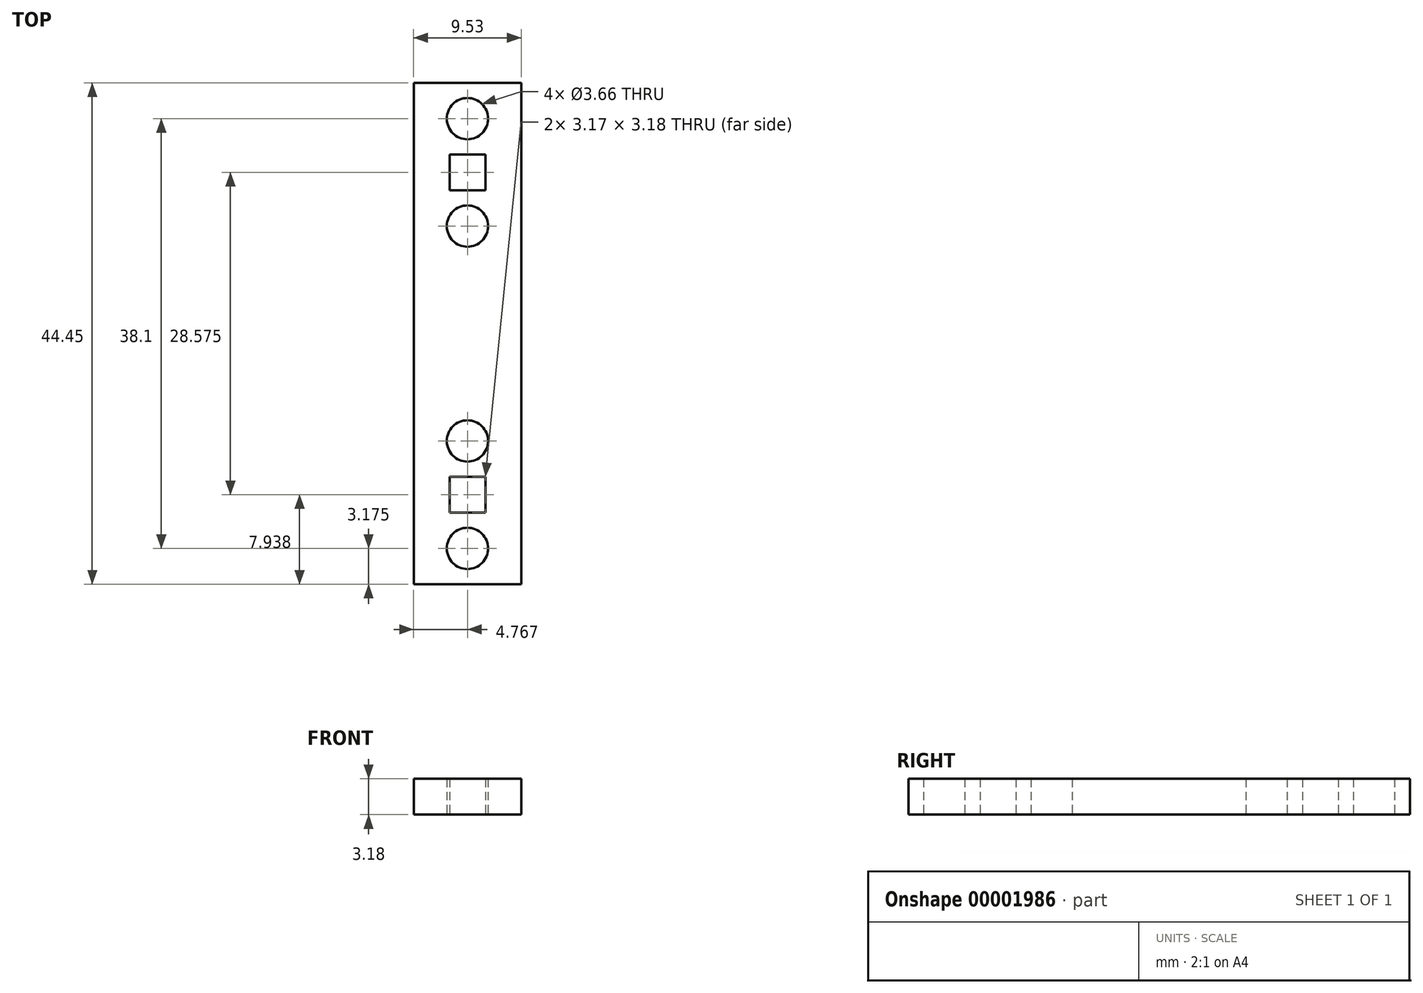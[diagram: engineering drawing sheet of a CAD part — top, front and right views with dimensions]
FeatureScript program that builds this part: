
annotation { "Feature Type Name" : "Feature", "Feature Type Description" : "" }
export const myFeature = defineFeature(function(context is Context, id is Id, definition is map)
    precondition{}
    {
        {
            var Q0;
            Q0=qCreatedBy(makeId("Top.planeOp"),FACE);
            var sketch = newSketch(context, id + "F0", { "sketchPlane" : qUnion([Q0])});
            skLineSegment(sketch, "E0", {"start": v(0, -6.35) * mm, "end": v(0, -38.1) * mm});
            skLineSegment(sketch, "E1", {"start": v(-3.18, -38.1) * mm, "end": v(-3.18, -34.93) * mm});
            skLineSegment(sketch, "E2", {"start": v(-3.18, -6.35) * mm, "end": v(-6.35, -6.35) * mm});
            skLineSegment(sketch, "E3", {"start": v(-6.35, -6.35) * mm, "end": v(-6.35, -9.52) * mm});
            skLineSegment(sketch, "E4", {"start": v(-9.52, -38.1) * mm, "end": v(-9.52, -6.35) * mm});
            skLineSegment(sketch, "E5", {"start": v(-9.52, -6.35) * mm, "end": v(-9.52, 0) * mm});
            skLineSegment(sketch, "E6", {"start": v(-9.52, 0) * mm, "end": v(0, 0) * mm});
            skLineSegment(sketch, "E7", {"start": v(-6.35, -9.52) * mm, "end": v(-3.18, -9.52) * mm});
            skLineSegment(sketch, "E8", {"start": v(-6.35, -38.1) * mm, "end": v(-3.18, -38.1) * mm});
            skLineSegment(sketch, "E9", {"start": v(-3.18, -34.93) * mm, "end": v(-6.35, -34.93) * mm});
            skLineSegment(sketch, "E10", {"start": v(-9.52, -38.1) * mm, "end": v(-9.52, -44.45) * mm});
            skLineSegment(sketch, "E11", {"start": v(-9.52, -44.45) * mm, "end": v(0, -44.45) * mm});
            skLineSegment(sketch, "E12", {"start": v(0, -6.35) * mm, "end": v(0, 0) * mm});
            skLineSegment(sketch, "E13", {"start": v(0, -38.1) * mm, "end": v(0, -44.45) * mm});
            skLineSegment(sketch, "E14.trimOffspring", {"start": v(-6.35, -34.93) * mm, "end": v(-6.35, -38.1) * mm});
            skLineSegment(sketch, "E15.trimOffspring", {"start": v(-3.18, -9.52) * mm, "end": v(-3.18, -6.35) * mm});
            skLineSegment(sketch, "E16", {"start": v(-9.52, -3.17) * mm, "end": v(-4.76, -3.17) * mm, "construction": true});
            skLineSegment(sketch, "E17", {"start": v(-4.76, -3.17) * mm, "end": v(0, -3.17) * mm, "construction": true});
            skCircle(sketch, "E18", {"center": v(-4.76, -3.17) * mm, "radius": 1.83 * mm});
            skLineSegment(sketch, "E19", {"start": v(0, -41.27) * mm, "end": v(-4.76, -41.27) * mm, "construction": true});
            skLineSegment(sketch, "E20", {"start": v(-4.76, -41.27) * mm, "end": v(-9.52, -41.27) * mm, "construction": true});
            skCircle(sketch, "E21", {"center": v(-4.76, -41.27) * mm, "radius": 1.83 * mm});
            skLineSegment(sketch, "E22", {"start": v(-4.76, -6.35) * mm, "end": v(-4.76, -3.17) * mm, "construction": true});
            skLineSegment(sketch, "E23", {"start": v(-4.76, -9.52) * mm, "end": v(-4.76, -12.7) * mm, "construction": true});
            skCircle(sketch, "E24", {"center": v(-4.76, -12.7) * mm, "radius": 1.83 * mm});
            skLineSegment(sketch, "E25", {"start": v(-4.76, -41.27) * mm, "end": v(-4.76, -38.1) * mm, "construction": true});
            skLineSegment(sketch, "E26", {"start": v(-4.76, -34.93) * mm, "end": v(-4.76, -31.75) * mm, "construction": true});
            skCircle(sketch, "E27", {"center": v(-4.76, -31.75) * mm, "radius": 1.83 * mm});
            skSolve(sketch);
        }
        {
            var Q0;
            Q0=makeQuery(id+"F0.imprint","IMPRINT",FACE,{"disambiguationData":[TD([[makeQuery(id+"F0.imprint","IMPRINT",EDGE,{"derivedFrom":sQuery(id+"F0.wireOp",EDGE,"E0")}),-1.0]])]});
            extrude(context, id + "F1", {"entities" : qUnion([Q0]), "depth" : 3.17 * mm});
        }
    });
